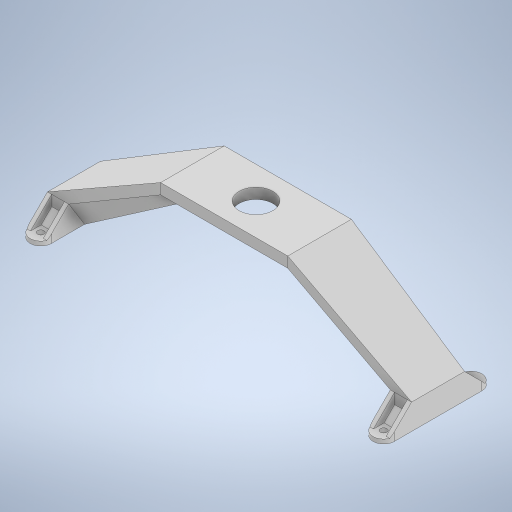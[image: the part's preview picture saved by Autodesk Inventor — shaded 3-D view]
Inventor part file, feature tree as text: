
AUTODESK INVENTOR PART (.ipt)
format: ipt  version: 2023 (Build 270158000, 158)  size: 454,144 bytes
history: native  units: in
note: dims shown in document units (in); Inventor stores cm internally (conversion verified against a paired STEP export)
features: sketch x6, extrude x6, other x6, chamfer x5, loft x4, mirror x1
ambient origin geometry x8: Origin, YZ Plane, XZ Plane, XY Plane, X Axis, Y Axis, Z Axis, Center Point
bodies: Solid1 (feature_tree)
feature tree (28):
  sketch  "Sketch1"  dims[d0=0.1181in d1=0.1181in]
  extrude  "Extrusion1"  Depth=0.1181in
  extrude  "Extrusion2"  Depth=0.1181in
  chamfer  "Chamfer1"  Distance=0.0787in
  chamfer  "Chamfer2"  Distance=0.9843in
  chamfer  "Chamfer3"  Distance=0.3209in
  chamfer  "Chamfer4"  Distance=1.626in
  chamfer  "Chamfer5"  Distance=0.9843in
  extrude  "Extrusion6"  Depth=0.3937in
  extrude  "Extrusion7"  Depth=0.3937in TaperAngle=0.0deg
  loft  "Loft5"
  extrude  "Extrusion8"  Depth=0.3937in
  loft  "Loft6"
  loft  "Loft7"
  loft  "Loft8"
  mirror  "Mirror3"
  extrude  "Extrusion10"  Depth=0.3937in TaperAngle=0.0deg
  sketch  "Sketch2"  dims[d2=0.1181in d3=0.1181in]
  sketch  "Sketch5"  dims[d4=0.3937in]
  other  "Edges12"
  other  "Edges13"
  sketch  "Sketch7"  dims[d5=0.3937in]
  sketch  "Sketch8"  dims[d6=0.3937in]
  other  "Edges14"
  other  "Edges15"
  other  "Edges16"
  other  "Edges17"
  sketch  "Sketch9"  dims[d7=0.3937in d8=0.0787in d9=0.0in d11=0.9843in d12=0.3209in d13=1.626in d14=0.9843in d15=0.3209in d16=0.3937in d17=0.0in d18=0.3937in d19=0.0787in d20=45.0deg d21=0.0in d22=0.0787in d23=0.315in d24=0.3937in d25=0.0787in d26=45.0deg d27=0.2362in d28=0.0787in d29=0.0in d30=0.3937in d31=0.0787in d32=45.0deg d33=0.315in d34=0.0787in d35=0.0in d36=0.3937in d37=0.0787in d38=45.0deg d39=0.0in d40=0.0787in d41=0.2362in d42=0.1969in d43=0.0787in d44=45.0deg d45=1.1811in d78=1.5748in d79=0.0in d80=2.3622in d81=1.1811in d82=0.1969in d83=0.0in d84=0.0in d85=90.0deg d86=0.0in d87=90.0deg d88=0.1969in d89=0.0in d93=0.1969in d94=0.3937in d95=0.1969in d96=0.4724in d97=0.3937in d98=0.0in d99=90.0deg d100=0.0in d101=90.0deg d102=0.0in d103=90.0deg d104=0.0in d105=90.0deg d106=0.0in d107=90.0deg d108=0.0in d109=90.0deg d110=0.625in d111=0.3937in d112=0.0in]
